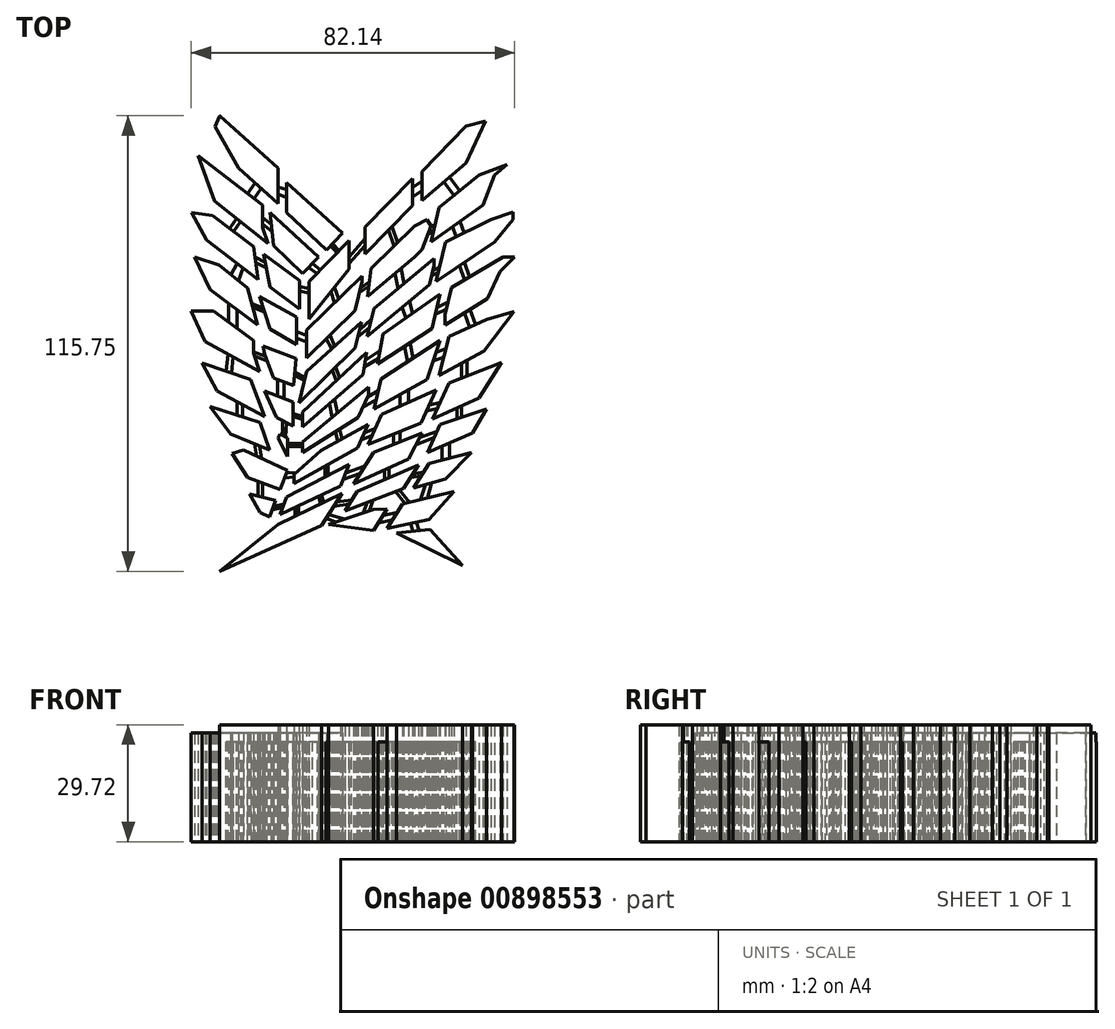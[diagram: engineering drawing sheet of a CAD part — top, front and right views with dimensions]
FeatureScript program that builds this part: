
annotation { "Feature Type Name" : "Feature", "Feature Type Description" : "" }
export const myFeature = defineFeature(function(context is Context, id is Id, definition is map)
    precondition{}
    {
        {
            var Q0;
            Q0=qCreatedBy(makeId("Top.planeOp"),FACE);
            var sketch = newSketch(context, id + "F0", { "sketchPlane" : qUnion([Q0])});
            skLineSegment(sketch, "E0", {"start": v(16.1, 33.24) * mm, "end": v(4.06, 20.9) * mm});
            skLineSegment(sketch, "E1", {"start": v(4.06, 20.9) * mm, "end": v(4.06, 27.82) * mm});
            skLineSegment(sketch, "E2", {"start": v(4.06, 27.82) * mm, "end": v(16.1, 40.16) * mm});
            skLineSegment(sketch, "E3", {"start": v(16.1, 40.16) * mm, "end": v(16.1, 33.24) * mm});
            skLineSegment(sketch, "E4", {"start": v(18.5, 34.46) * mm, "end": v(29.69, 44) * mm});
            skLineSegment(sketch, "E5", {"start": v(29.69, 44) * mm, "end": v(34.61, 54.74) * mm});
            skLineSegment(sketch, "E6", {"start": v(34.61, 54.74) * mm, "end": v(29.69, 53.4) * mm});
            skLineSegment(sketch, "E7", {"start": v(29.69, 53.4) * mm, "end": v(18.5, 41.94) * mm});
            skLineSegment(sketch, "E8", {"start": v(18.5, 41.94) * mm, "end": v(18.5, 34.46) * mm});
            skLineSegment(sketch, "E9", {"start": v(0, 17.06) * mm, "end": v(0, 24.37) * mm});
            skLineSegment(sketch, "E10", {"start": v(0, 24.37) * mm, "end": v(-10.2, 13.91) * mm});
            skLineSegment(sketch, "E11", {"start": v(-10.2, 13.91) * mm, "end": v(-10.2, 4.4) * mm});
            skLineSegment(sketch, "E12", {"start": v(-10.2, 4.4) * mm, "end": v(0, 17.06) * mm});
            skLineSegment(sketch, "E13", {"start": v(3.27, 13.98) * mm, "end": v(1.51, 6.57) * mm});
            skLineSegment(sketch, "E14", {"start": v(1.51, 6.57) * mm, "end": v(-10.85, -5.49) * mm});
            skLineSegment(sketch, "E15", {"start": v(-10.85, -5.49) * mm, "end": v(-10.85, 1.62) * mm});
            skLineSegment(sketch, "E16", {"start": v(-10.85, 1.62) * mm, "end": v(3.27, 15.38) * mm});
            skLineSegment(sketch, "E17", {"start": v(3.27, 15.38) * mm, "end": v(3.27, 13.98) * mm});
            skLineSegment(sketch, "E18", {"start": v(16.55, 28) * mm, "end": v(5.55, 17.27) * mm});
            skLineSegment(sketch, "E19", {"start": v(5.55, 17.27) * mm, "end": v(4.6, 10.07) * mm});
            skLineSegment(sketch, "E20", {"start": v(4.6, 10.07) * mm, "end": v(16.55, 20.16) * mm});
            skLineSegment(sketch, "E21", {"start": v(16.55, 20.16) * mm, "end": v(18.49, 22.05) * mm});
            skLineSegment(sketch, "E22", {"start": v(18.49, 22.05) * mm, "end": v(20.78, 28) * mm});
            skLineSegment(sketch, "E23", {"start": v(20.78, 28) * mm, "end": v(19.75, 29.75) * mm});
            skLineSegment(sketch, "E24", {"start": v(22.84, 32.73) * mm, "end": v(20.78, 24) * mm});
            skLineSegment(sketch, "E25", {"start": v(20.78, 24) * mm, "end": v(34.05, 33.4) * mm});
            skLineSegment(sketch, "E26", {"start": v(34.05, 33.4) * mm, "end": v(36.97, 40.99) * mm});
            skLineSegment(sketch, "E27", {"start": v(36.97, 40.99) * mm, "end": v(40.07, 43.63) * mm});
            skLineSegment(sketch, "E28", {"start": v(40.07, 43.63) * mm, "end": v(32.98, 40.99) * mm});
            skLineSegment(sketch, "E29", {"start": v(32.98, 40.99) * mm, "end": v(22.84, 32.73) * mm});
            skLineSegment(sketch, "E30", {"start": v(24.46, 24) * mm, "end": v(22.1, 13.98) * mm});
            skLineSegment(sketch, "E31", {"start": v(22.1, 13.98) * mm, "end": v(36.97, 24) * mm});
            skLineSegment(sketch, "E32", {"start": v(36.97, 24) * mm, "end": v(41.6, 29.75) * mm});
            skLineSegment(sketch, "E33", {"start": v(24.46, 24) * mm, "end": v(36, 29.75) * mm});
            skLineSegment(sketch, "E34", {"start": v(36, 29.75) * mm, "end": v(41.6, 31.62) * mm});
            skLineSegment(sketch, "E35", {"start": v(41.6, 31.62) * mm, "end": v(41.6, 29.75) * mm});
            skLineSegment(sketch, "E36", {"start": v(6.35, 7.12) * mm, "end": v(4.57, 0) * mm});
            skLineSegment(sketch, "E37", {"start": v(4.57, 0) * mm, "end": v(20.38, 13.16) * mm});
            skLineSegment(sketch, "E38", {"start": v(20.38, 13.16) * mm, "end": v(21.53, 18.02) * mm});
            skLineSegment(sketch, "E39", {"start": v(21.53, 18.02) * mm, "end": v(21.53, 19.72) * mm});
            skLineSegment(sketch, "E40", {"start": v(21.53, 19.72) * mm, "end": v(6.35, 7.12) * mm});
            skLineSegment(sketch, "E41", {"start": v(-10.85, -8.86) * mm, "end": v(-12.74, -16.88) * mm});
            skLineSegment(sketch, "E42", {"start": v(-12.74, -16.88) * mm, "end": v(1.52, -2.98) * mm});
            skLineSegment(sketch, "E43", {"start": v(1.52, -2.98) * mm, "end": v(3.1, 3.67) * mm});
            skLineSegment(sketch, "E44", {"start": v(3.1, 3.67) * mm, "end": v(-10.85, -8.86) * mm});
            skLineSegment(sketch, "E45", {"start": v(4.35, -4.15) * mm, "end": v(-11.88, -19.15) * mm});
            skLineSegment(sketch, "E46", {"start": v(-11.88, -19.15) * mm, "end": v(-11.88, -23.05) * mm});
            skLineSegment(sketch, "E47", {"start": v(-11.88, -23.05) * mm, "end": v(3.53, -9.7) * mm});
            skLineSegment(sketch, "E48", {"start": v(3.53, -9.7) * mm, "end": v(4.35, -4.15) * mm});
            skLineSegment(sketch, "E49", {"start": v(7.23, -7.03) * mm, "end": v(21, 2.01) * mm});
            skLineSegment(sketch, "E50", {"start": v(21, 2.01) * mm, "end": v(23.06, 10.75) * mm});
            skLineSegment(sketch, "E51", {"start": v(23.06, 10.75) * mm, "end": v(8.65, 0.6) * mm});
            skLineSegment(sketch, "E52", {"start": v(8.65, 0.6) * mm, "end": v(7.23, -7.03) * mm});
            skLineSegment(sketch, "E53", {"start": v(26.04, 12.46) * mm, "end": v(24.4, 5.55) * mm});
            skLineSegment(sketch, "E54", {"start": v(24.4, 5.55) * mm, "end": v(24.4, 2.84) * mm});
            skLineSegment(sketch, "E55", {"start": v(24.4, 2.84) * mm, "end": v(35.15, 9.68) * mm});
            skLineSegment(sketch, "E56", {"start": v(35.15, 9.68) * mm, "end": v(36.57, 12.76) * mm});
            skLineSegment(sketch, "E57", {"start": v(36.57, 12.76) * mm, "end": v(38.28, 16.49) * mm});
            skLineSegment(sketch, "E58", {"start": v(38.28, 16.49) * mm, "end": v(42.02, 20.14) * mm});
            skLineSegment(sketch, "E59", {"start": v(42.02, 20.14) * mm, "end": v(39.02, 20.14) * mm});
            skLineSegment(sketch, "E60", {"start": v(39.02, 20.14) * mm, "end": v(26.04, 12.46) * mm});
            skLineSegment(sketch, "E61", {"start": v(-11.84, -29.54) * mm, "end": v(2.25, -20.58) * mm});
            skLineSegment(sketch, "E62", {"start": v(2.25, -20.58) * mm, "end": v(4.88, -14.85) * mm});
            skLineSegment(sketch, "E63", {"start": v(4.88, -14.85) * mm, "end": v(4.88, -12.89) * mm});
            skLineSegment(sketch, "E64", {"start": v(4.88, -12.89) * mm, "end": v(-11.86, -26.82) * mm});
            skLineSegment(sketch, "E65", {"start": v(8.15, -10.8) * mm, "end": v(6.36, -18.42) * mm});
            skLineSegment(sketch, "E66", {"start": v(6.36, -18.42) * mm, "end": v(19.76, -10.9) * mm});
            skLineSegment(sketch, "E67", {"start": v(19.76, -10.9) * mm, "end": v(23.06, -1.06) * mm});
            skLineSegment(sketch, "E68", {"start": v(23.06, -1.06) * mm, "end": v(8.15, -10.8) * mm});
            skLineSegment(sketch, "E69", {"start": v(25.35, 0) * mm, "end": v(22.87, -9.98) * mm});
            skLineSegment(sketch, "E70", {"start": v(22.87, -9.98) * mm, "end": v(34.26, -3.66) * mm});
            skLineSegment(sketch, "E71", {"start": v(34.26, -3.66) * mm, "end": v(41.93, 6.3) * mm});
            skLineSegment(sketch, "E72", {"start": v(41.93, 6.3) * mm, "end": v(34.89, 4.32) * mm});
            skLineSegment(sketch, "E73", {"start": v(34.89, 4.32) * mm, "end": v(25.35, 0) * mm});
            skLineSegment(sketch, "E74", {"start": v(-14, -37.38) * mm, "end": v(2.06, -28.36) * mm});
            skLineSegment(sketch, "E75", {"start": v(2.06, -28.36) * mm, "end": v(4.81, -22.38) * mm});
            skLineSegment(sketch, "E76", {"start": v(4.81, -22.38) * mm, "end": v(-7.2, -28.98) * mm});
            skLineSegment(sketch, "E77", {"start": v(-7.2, -28.98) * mm, "end": v(-14, -35.04) * mm});
            skLineSegment(sketch, "E78", {"start": v(-14, -35.04) * mm, "end": v(-14, -37.38) * mm});
            skLineSegment(sketch, "E79", {"start": v(8.24, -19.84) * mm, "end": v(4.76, -27.42) * mm});
            skLineSegment(sketch, "E80", {"start": v(4.76, -27.42) * mm, "end": v(18.25, -22.06) * mm});
            skLineSegment(sketch, "E81", {"start": v(18.25, -22.06) * mm, "end": v(22.1, -13.66) * mm});
            skLineSegment(sketch, "E82", {"start": v(22.1, -13.66) * mm, "end": v(8.24, -19.84) * mm});
            skLineSegment(sketch, "E83", {"start": v(25.35, -11.8) * mm, "end": v(21.15, -20.96) * mm});
            skLineSegment(sketch, "E84", {"start": v(21.15, -20.96) * mm, "end": v(32.96, -15.63) * mm});
            skLineSegment(sketch, "E85", {"start": v(32.96, -15.63) * mm, "end": v(38.64, -6.61) * mm});
            skLineSegment(sketch, "E86", {"start": v(38.64, -6.61) * mm, "end": v(25.35, -11.8) * mm});
            skLineSegment(sketch, "E87", {"start": v(-11.86, -26.82) * mm, "end": v(-11.84, -29.54) * mm});
            skLineSegment(sketch, "E88", {"start": v(-15.86, -40.84) * mm, "end": v(-17.59, -45.3) * mm});
            skLineSegment(sketch, "E89", {"start": v(-17.59, -45.3) * mm, "end": v(-2.26, -38) * mm});
            skLineSegment(sketch, "E90", {"start": v(-2.26, -38) * mm, "end": v(0, -32.56) * mm});
            skLineSegment(sketch, "E91", {"start": v(0, -32.56) * mm, "end": v(-15.86, -40.84) * mm});
            skLineSegment(sketch, "E92", {"start": v(6.14, -29.54) * mm, "end": v(1.07, -37.5) * mm});
            skLineSegment(sketch, "E93", {"start": v(1.07, -37.5) * mm, "end": v(15.04, -31.2) * mm});
            skLineSegment(sketch, "E94", {"start": v(15.04, -31.2) * mm, "end": v(18.5, -24.53) * mm});
            skLineSegment(sketch, "E95", {"start": v(18.5, -24.53) * mm, "end": v(6.14, -29.54) * mm});
            skLineSegment(sketch, "E96", {"start": v(23.07, -22.43) * mm, "end": v(19.86, -29.54) * mm});
            skLineSegment(sketch, "E97", {"start": v(19.86, -29.54) * mm, "end": v(31.35, -24.53) * mm});
            skLineSegment(sketch, "E98", {"start": v(31.35, -24.53) * mm, "end": v(34.93, -18.48) * mm});
            skLineSegment(sketch, "E99", {"start": v(34.93, -18.48) * mm, "end": v(23.07, -22.43) * mm});
            skLineSegment(sketch, "E100", {"start": v(-18.13, -47.75) * mm, "end": v(-32.87, -59.68) * mm});
            skLineSegment(sketch, "E101", {"start": v(-32.87, -59.68) * mm, "end": v(-6.98, -48) * mm});
            skLineSegment(sketch, "E102", {"start": v(-6.98, -48) * mm, "end": v(-1.85, -39.94) * mm});
            skLineSegment(sketch, "E103", {"start": v(-1.85, -39.94) * mm, "end": v(-18.13, -47.75) * mm});
            skLineSegment(sketch, "E104", {"start": v(2.02, -39.4) * mm, "end": v(-1.11, -44.32) * mm});
            skLineSegment(sketch, "E105", {"start": v(-1.11, -44.32) * mm, "end": v(13.81, -38.66) * mm});
            skLineSegment(sketch, "E106", {"start": v(13.81, -38.66) * mm, "end": v(17.6, -32.7) * mm});
            skLineSegment(sketch, "E107", {"start": v(17.6, -32.7) * mm, "end": v(2.02, -39.4) * mm});
            skLineSegment(sketch, "E108", {"start": v(20.33, -32.27) * mm, "end": v(16.34, -38.54) * mm});
            skLineSegment(sketch, "E109", {"start": v(16.34, -38.54) * mm, "end": v(24.5, -36.2) * mm});
            skLineSegment(sketch, "E110", {"start": v(24.5, -36.2) * mm, "end": v(31.02, -29.54) * mm});
            skLineSegment(sketch, "E111", {"start": v(31.02, -29.54) * mm, "end": v(20.33, -32.27) * mm});
            skLineSegment(sketch, "E112", {"start": v(9.64, -43.82) * mm, "end": v(6.14, -49.32) * mm});
            skLineSegment(sketch, "E113", {"start": v(6.14, -49.32) * mm, "end": v(-5.23, -47.75) * mm});
            skLineSegment(sketch, "E114", {"start": v(-5.23, -47.75) * mm, "end": v(6.14, -43.94) * mm});
            skLineSegment(sketch, "E115", {"start": v(6.14, -43.94) * mm, "end": v(9.64, -43.82) * mm});
            skLineSegment(sketch, "E116", {"start": v(13.57, -42.6) * mm, "end": v(9.64, -48.78) * mm});
            skLineSegment(sketch, "E117", {"start": v(9.64, -48.78) * mm, "end": v(20.33, -46.52) * mm});
            skLineSegment(sketch, "E118", {"start": v(20.33, -46.52) * mm, "end": v(26.6, -39.4) * mm});
            skLineSegment(sketch, "E119", {"start": v(26.6, -39.4) * mm, "end": v(13.57, -42.6) * mm});
            skLineSegment(sketch, "E120", {"start": v(-34.07, 53.36) * mm, "end": v(-28.12, 42.75) * mm});
            skLineSegment(sketch, "E121", {"start": v(-28.12, 42.75) * mm, "end": v(-18.13, 33.7) * mm});
            skLineSegment(sketch, "E122", {"start": v(-18.13, 33.7) * mm, "end": v(-18.13, 42.8) * mm});
            skLineSegment(sketch, "E123", {"start": v(-18.13, 42.8) * mm, "end": v(-32.88, 56.07) * mm});
            skLineSegment(sketch, "E124", {"start": v(-32.88, 56.07) * mm, "end": v(-34.07, 53.36) * mm});
            skLineSegment(sketch, "E125", {"start": v(-15.86, 39.07) * mm, "end": v(-15.86, 31.48) * mm});
            skLineSegment(sketch, "E126", {"start": v(-15.86, 31.48) * mm, "end": v(-5.79, 21.95) * mm});
            skLineSegment(sketch, "E127", {"start": v(-5.79, 21.95) * mm, "end": v(-1.74, 26.22) * mm});
            skLineSegment(sketch, "E128", {"start": v(-1.74, 26.22) * mm, "end": v(-15.86, 39.07) * mm});
            skLineSegment(sketch, "E129", {"start": v(-20.08, 31.48) * mm, "end": v(-7.72, 20.16) * mm});
            skLineSegment(sketch, "E130", {"start": v(-7.72, 20.16) * mm, "end": v(-11.84, 15.94) * mm});
            skLineSegment(sketch, "E131", {"start": v(-11.84, 15.94) * mm, "end": v(-19.21, 23.13) * mm});
            skLineSegment(sketch, "E132", {"start": v(-19.21, 23.13) * mm, "end": v(-20.08, 31.48) * mm});
            skLineSegment(sketch, "E133", {"start": v(-34.22, 34.33) * mm, "end": v(-38.4, 45.92) * mm});
            skLineSegment(sketch, "E134", {"start": v(-22.01, 27.63) * mm, "end": v(-20.55, 23.57) * mm});
            skLineSegment(sketch, "E135", {"start": v(-20.55, 23.57) * mm, "end": v(-34.22, 34.33) * mm});
            skLineSegment(sketch, "E136", {"start": v(-22.01, 27.63) * mm, "end": v(-22.01, 33.36) * mm});
            skLineSegment(sketch, "E137", {"start": v(-22.01, 33.36) * mm, "end": v(-38.4, 45.92) * mm});
            skLineSegment(sketch, "E138", {"start": v(-24.3, 22.86) * mm, "end": v(-23.16, 14.47) * mm});
            skLineSegment(sketch, "E139", {"start": v(-23.16, 14.47) * mm, "end": v(-36.23, 24.45) * mm});
            skLineSegment(sketch, "E140", {"start": v(-36.23, 24.45) * mm, "end": v(-40.02, 31.51) * mm});
            skLineSegment(sketch, "E141", {"start": v(-40.02, 31.51) * mm, "end": v(-34.73, 30.72) * mm});
            skLineSegment(sketch, "E142", {"start": v(-34.73, 30.72) * mm, "end": v(-24.3, 22.86) * mm});
            skLineSegment(sketch, "E143", {"start": v(-21.72, 20.9) * mm, "end": v(-20.13, 12.57) * mm});
            skLineSegment(sketch, "E144", {"start": v(-20.13, 12.57) * mm, "end": v(-12.65, 6.93) * mm});
            skLineSegment(sketch, "E145", {"start": v(-12.65, 6.93) * mm, "end": v(-12.65, 14.16) * mm});
            skLineSegment(sketch, "E146", {"start": v(-12.65, 14.16) * mm, "end": v(-21.72, 20.9) * mm});
            skLineSegment(sketch, "E147", {"start": v(-22.78, 10.1) * mm, "end": v(-20.13, 1.88) * mm});
            skLineSegment(sketch, "E148", {"start": v(-20.13, 1.88) * mm, "end": v(-13.4, -2.01) * mm});
            skLineSegment(sketch, "E149", {"start": v(-13.4, -2.01) * mm, "end": v(-13.4, 4.88) * mm});
            skLineSegment(sketch, "E150", {"start": v(-13.4, 4.88) * mm, "end": v(-22.78, 10.1) * mm});
            skLineSegment(sketch, "E151", {"start": v(-25.78, 12.3) * mm, "end": v(-23.3, 2.87) * mm});
            skLineSegment(sketch, "E152", {"start": v(-23.3, 2.87) * mm, "end": v(-35.28, 11.91) * mm});
            skLineSegment(sketch, "E153", {"start": v(-35.28, 11.91) * mm, "end": v(-39.33, 20.22) * mm});
            skLineSegment(sketch, "E154", {"start": v(-39.33, 20.22) * mm, "end": v(-33.04, 18.07) * mm});
            skLineSegment(sketch, "E155", {"start": v(-33.04, 18.07) * mm, "end": v(-25.78, 12.3) * mm});
            skLineSegment(sketch, "E156", {"start": v(-24.3, -4.2) * mm, "end": v(-22.78, -8.95) * mm});
            skLineSegment(sketch, "E157", {"start": v(-22.78, -8.95) * mm, "end": v(-36.62, -1.25) * mm});
            skLineSegment(sketch, "E158", {"start": v(-36.62, -1.25) * mm, "end": v(-40.12, 6.45) * mm});
            skLineSegment(sketch, "E159", {"start": v(-40.12, 6.45) * mm, "end": v(-34.4, 6.45) * mm});
            skLineSegment(sketch, "E160", {"start": v(-34.4, 6.45) * mm, "end": v(-24.3, -1.06) * mm});
            skLineSegment(sketch, "E161", {"start": v(-24.3, -1.06) * mm, "end": v(-24.3, -4.2) * mm});
            skLineSegment(sketch, "E162", {"start": v(-21.55, -4.41) * mm, "end": v(-19.24, -10.6) * mm});
            skLineSegment(sketch, "E163", {"start": v(-19.24, -10.6) * mm, "end": v(-14.15, -12.46) * mm});
            skLineSegment(sketch, "E164", {"start": v(-14.15, -12.46) * mm, "end": v(-13.5, -5.62) * mm});
            skLineSegment(sketch, "E165", {"start": v(-13.5, -5.62) * mm, "end": v(-21.82, -2.38) * mm});
            skLineSegment(sketch, "E166", {"start": v(-21.82, -2.38) * mm, "end": v(-21.55, -4.41) * mm});
            skLineSegment(sketch, "E167", {"start": v(-21.55, -13.86) * mm, "end": v(-18.48, -20.65) * mm});
            skLineSegment(sketch, "E168", {"start": v(-18.48, -20.65) * mm, "end": v(-14.3, -22.8) * mm});
            skLineSegment(sketch, "E169", {"start": v(-14.3, -16.62) * mm, "end": v(-21.55, -13.86) * mm});
            skLineSegment(sketch, "E170", {"start": v(-37.4, -6.81) * mm, "end": v(-33.52, -13.86) * mm});
            skLineSegment(sketch, "E171", {"start": v(-33.52, -13.86) * mm, "end": v(-21.55, -20.4) * mm});
            skLineSegment(sketch, "E172", {"start": v(-21.55, -20.4) * mm, "end": v(-25.12, -10.95) * mm});
            skLineSegment(sketch, "E173", {"start": v(-25.12, -10.95) * mm, "end": v(-37.4, -6.81) * mm});
            skLineSegment(sketch, "E174", {"start": v(-17.57, -24.82) * mm, "end": v(-15.6, -25.84) * mm});
            skLineSegment(sketch, "E175", {"start": v(-15.6, -25.84) * mm, "end": v(-15.6, -30.49) * mm});
            skLineSegment(sketch, "E176", {"start": v(-17.57, -24.82) * mm, "end": v(-18.1, -25.87) * mm});
            skLineSegment(sketch, "E177", {"start": v(-18.1, -25.87) * mm, "end": v(-15.6, -30.49) * mm});
            skLineSegment(sketch, "E178", {"start": v(-20.25, -28.9) * mm, "end": v(-22.65, -21.85) * mm});
            skLineSegment(sketch, "E179", {"start": v(-22.65, -21.85) * mm, "end": v(-35.36, -17.78) * mm});
            skLineSegment(sketch, "E180", {"start": v(-35.36, -17.78) * mm, "end": v(-30.13, -24.82) * mm});
            skLineSegment(sketch, "E181", {"start": v(-30.13, -24.82) * mm, "end": v(-20.25, -28.9) * mm});
            skLineSegment(sketch, "E182", {"start": v(-15.6, -34.12) * mm, "end": v(-17.57, -38.88) * mm});
            skLineSegment(sketch, "E183", {"start": v(-17.57, -38.88) * mm, "end": v(-25.8, -35.89) * mm});
            skLineSegment(sketch, "E184", {"start": v(-25.8, -35.89) * mm, "end": v(-29.78, -29.8) * mm});
            skLineSegment(sketch, "E185", {"start": v(-29.78, -29.8) * mm, "end": v(-26.8, -28.9) * mm});
            skLineSegment(sketch, "E186", {"start": v(-26.8, -28.9) * mm, "end": v(-15.6, -34.12) * mm});
            skLineSegment(sketch, "E187", {"start": v(-18.73, -41.72) * mm, "end": v(-20.25, -45.91) * mm});
            skLineSegment(sketch, "E188", {"start": v(-20.25, -45.91) * mm, "end": v(-22.6, -44.7) * mm});
            skLineSegment(sketch, "E189", {"start": v(-22.6, -44.7) * mm, "end": v(-25.25, -39.97) * mm});
            skLineSegment(sketch, "E190", {"start": v(-25.25, -39.97) * mm, "end": v(-18.73, -41.72) * mm});
            skLineSegment(sketch, "E191", {"start": v(11.97, -49.96) * mm, "end": v(20.57, -49.05) * mm});
            skLineSegment(sketch, "E192", {"start": v(20.57, -49.05) * mm, "end": v(28.76, -58.25) * mm});
            skLineSegment(sketch, "E193", {"start": v(28.76, -58.25) * mm, "end": v(11.97, -49.96) * mm});
            skLineSegment(sketch, "E194", {"start": v(-11.88, -23.05) * mm, "end": v(-11.86, -26.82) * mm});
            skLineSegment(sketch, "E195", {"start": v(-12.74, -16.88) * mm, "end": v(-11.88, -19.15) * mm});
            skLineSegment(sketch, "E196", {"start": v(-10.68, -5.38) * mm, "end": v(-10.85, -8.86) * mm});
            skLineSegment(sketch, "E197", {"start": v(-14, -37.38) * mm, "end": v(-15.86, -40.84) * mm});
            skLineSegment(sketch, "E198", {"start": v(16.55, 28) * mm, "end": v(19.75, 29.75) * mm});
            skLineSegment(sketch, "E199", {"start": v(4.57, 0) * mm, "end": v(1.52, -2.98) * mm});
            skLineSegment(sketch, "E200", {"start": v(22.1, -13.66) * mm, "end": v(25.35, -11.8) * mm});
            skLineSegment(sketch, "E201", {"start": v(-17.59, -45.3) * mm, "end": v(-18.13, -47.75) * mm});
            skLineSegment(sketch, "E202", {"start": v(24.4, 2.84) * mm, "end": v(25.35, 0) * mm});
            skLineSegment(sketch, "E203", {"start": v(-14.3, -16.62) * mm, "end": v(-14.3, -22.8) * mm});
            skLineSegment(sketch, "E204.bottom", {"start": v(-32.9, 56.04) * mm, "end": v(-32.85, 56.04) * mm});
            skSolve(sketch);
        }
        {
            var Q0;
            Q0=makeQuery(id+"F0.imprint","IMPRINT",FACE,{"disambiguationData":[TD([[makeQuery(id+"F0.imprint","IMPRINT",EDGE,{"derivedFrom":sQuery(id+"F0.wireOp",EDGE,"E170")}),1.0]])]});
            var Q1;
            Q1=makeQuery(id+"F0.imprint","IMPRINT",FACE,{"disambiguationData":[TD([[makeQuery(id+"F0.imprint","IMPRINT",EDGE,{"derivedFrom":sQuery(id+"F0.wireOp",EDGE,"E191")}),-1.0]])]});
            var Q2;
            Q2=makeQuery(id+"F0.imprint","IMPRINT",FACE,{"disambiguationData":[TD([[makeQuery(id+"F0.imprint","IMPRINT",EDGE,{"derivedFrom":sQuery(id+"F0.wireOp",EDGE,"E4")}),1.0]])]});
            var Q3;
            Q3=makeQuery(id+"F0.imprint","IMPRINT",FACE,{"disambiguationData":[TD([[makeQuery(id+"F0.imprint","IMPRINT",EDGE,{"derivedFrom":sQuery(id+"F0.wireOp",EDGE,"E69")}),1.0]])]});
            var Q4;
            Q4=makeQuery(id+"F0.imprint","IMPRINT",FACE,{"disambiguationData":[TD([[makeQuery(id+"F0.imprint","IMPRINT",EDGE,{"derivedFrom":sQuery(id+"F0.wireOp",EDGE,"E83")}),1.0]])]});
            var Q5;
            Q5=makeQuery(id+"F0.imprint","IMPRINT",FACE,{"disambiguationData":[TD([[makeQuery(id+"F0.imprint","IMPRINT",EDGE,{"derivedFrom":sQuery(id+"F0.wireOp",EDGE,"E96")}),1.0]])]});
            var Q6;
            Q6=makeQuery(id+"F0.imprint","IMPRINT",FACE,{"disambiguationData":[TD([[makeQuery(id+"F0.imprint","IMPRINT",EDGE,{"derivedFrom":sQuery(id+"F0.wireOp",EDGE,"E100")}),1.0]])]});
            var Q7;
            Q7=makeQuery(id+"F0.imprint","IMPRINT",FACE,{"disambiguationData":[TD([[makeQuery(id+"F0.imprint","IMPRINT",EDGE,{"derivedFrom":sQuery(id+"F0.wireOp",EDGE,"E108")}),1.0]])]});
            var Q8;
            Q8=makeQuery(id+"F0.imprint","IMPRINT",FACE,{"disambiguationData":[TD([[makeQuery(id+"F0.imprint","IMPRINT",EDGE,{"derivedFrom":sQuery(id+"F0.wireOp",EDGE,"E112")}),-1.0]])]});
            var Q9;
            Q9=makeQuery(id+"F0.imprint","IMPRINT",FACE,{"disambiguationData":[TD([[makeQuery(id+"F0.imprint","IMPRINT",EDGE,{"derivedFrom":sQuery(id+"F0.wireOp",EDGE,"E116")}),1.0]])]});
            var Q10;
            Q10=makeQuery(id+"F0.imprint","IMPRINT",FACE,{"disambiguationData":[TD([[makeQuery(id+"F0.imprint","IMPRINT",EDGE,{"derivedFrom":sQuery(id+"F0.wireOp",EDGE,"E120")}),1.0]])]});
            var Q11;
            Q11=makeQuery(id+"F0.imprint","IMPRINT",FACE,{"disambiguationData":[TD([[makeQuery(id+"F0.imprint","IMPRINT",EDGE,{"derivedFrom":sQuery(id+"F0.wireOp",EDGE,"E156")}),-1.0]])]});
            var Q12;
            Q12=makeQuery(id+"F0.imprint","IMPRINT",FACE,{"disambiguationData":[TD([[makeQuery(id+"F0.imprint","IMPRINT",EDGE,{"derivedFrom":sQuery(id+"F0.wireOp",EDGE,"E178")}),1.0]])]});
            var Q13;
            Q13=makeQuery(id+"F0.imprint","IMPRINT",FACE,{"disambiguationData":[TD([[makeQuery(id+"F0.imprint","IMPRINT",EDGE,{"derivedFrom":sQuery(id+"F0.wireOp",EDGE,"E187")}),-1.0]])]});
            var Q14;
            Q14=makeQuery(id+"F0.imprint","IMPRINT",FACE,{"disambiguationData":[TD([[makeQuery(id+"F0.imprint","IMPRINT",EDGE,{"derivedFrom":sQuery(id+"F0.wireOp",EDGE,"E0")}),-1.0]])]});
            var Q15;
            Q15=makeQuery(id+"F0.imprint","IMPRINT",FACE,{"disambiguationData":[TD([[makeQuery(id+"F0.imprint","IMPRINT",EDGE,{"derivedFrom":sQuery(id+"F0.wireOp",EDGE,"E24")}),1.0]])]});
            var Q16;
            Q16=makeQuery(id+"F0.imprint","IMPRINT",FACE,{"disambiguationData":[TD([[makeQuery(id+"F0.imprint","IMPRINT",EDGE,{"derivedFrom":sQuery(id+"F0.wireOp",EDGE,"E30")}),1.0]])]});
            var Q17;
            Q17=makeQuery(id+"F0.imprint","IMPRINT",FACE,{"disambiguationData":[TD([[makeQuery(id+"F0.imprint","IMPRINT",EDGE,{"derivedFrom":sQuery(id+"F0.wireOp",EDGE,"E53")}),1.0]])]});
            var Q18;
            Q18=makeQuery(id+"F0.imprint","IMPRINT",FACE,{"disambiguationData":[TD([[makeQuery(id+"F0.imprint","IMPRINT",EDGE,{"derivedFrom":sQuery(id+"F0.wireOp",EDGE,"E125")}),1.0]])]});
            var Q19;
            {var subQ1=sQuery(id+"F0.wireOp",EDGE,"E133");Q19=makeQuery(id+"F0.imprint","IMPRINT",FACE,{"disambiguationData":[TD([[makeQuery(id+"F0.imprint","IMPRINT",EDGE,{"derivedFrom":subQ1}),-1.0]])]});}
            var Q20;
            Q20=makeQuery(id+"F0.imprint","IMPRINT",FACE,{"disambiguationData":[TD([[makeQuery(id+"F0.imprint","IMPRINT",EDGE,{"derivedFrom":sQuery(id+"F0.wireOp",EDGE,"E138")}),-1.0]])]});
            var Q21;
            Q21=makeQuery(id+"F0.imprint","IMPRINT",FACE,{"disambiguationData":[TD([[makeQuery(id+"F0.imprint","IMPRINT",EDGE,{"derivedFrom":sQuery(id+"F0.wireOp",EDGE,"E151")}),-1.0]])]});
            var Q22;
            Q22=makeQuery(id+"F0.imprint","IMPRINT",FACE,{"disambiguationData":[TD([[makeQuery(id+"F0.imprint","IMPRINT",EDGE,{"derivedFrom":sQuery(id+"F0.wireOp",EDGE,"E182")}),-1.0]])]});
            var Q23;
            Q23=makeQuery(id+"F0.imprint","IMPRINT",FACE,{"disambiguationData":[TD([[makeQuery(id+"F0.imprint","IMPRINT",EDGE,{"derivedFrom":sQuery(id+"F0.wireOp",EDGE,"E88")}),-1.0]])]});
            var Q24;
            Q24=makeQuery(id+"F0.imprint","IMPRINT",FACE,{"disambiguationData":[TD([[makeQuery(id+"F0.imprint","IMPRINT",EDGE,{"derivedFrom":sQuery(id+"F0.wireOp",EDGE,"Hd1NYOsB-rz69-P5dz-xRzD-SZfXTA0eVR0r")}),-1.0]])]});
            var Q25;
            Q25=makeQuery(id+"F0.imprint","IMPRINT",FACE,{"disambiguationData":[TD([[makeQuery(id+"F0.imprint","IMPRINT",EDGE,{"derivedFrom":sQuery(id+"F0.wireOp",EDGE,"LXoHO3Um-HMFk-hWAO-TxCi-RrEVqA140TyF")}),-1.0]])]});
            var Q26;
            Q26=makeQuery(id+"F0.imprint","IMPRINT",FACE,{"disambiguationData":[TD([[makeQuery(id+"F0.imprint","IMPRINT",EDGE,{"derivedFrom":sQuery(id+"F0.wireOp",EDGE,"s4iQujFb-FTHa-1j17-edHK-8T7tGA8HVips")}),-1.0]])]});
            var Q27;
            Q27=makeQuery(id+"F0.imprint","IMPRINT",FACE,{"disambiguationData":[TD([[makeQuery(id+"F0.imprint","IMPRINT",EDGE,{"derivedFrom":sQuery(id+"F0.wireOp",EDGE,"Gbdayy7W-T8TN-iNEz-qSY6-jhz4T1zxVgPG")}),1.0]])]});
            var Q28;
            Q28=makeQuery(id+"F0.imprint","IMPRINT",FACE,{"disambiguationData":[TD([[makeQuery(id+"F0.imprint","IMPRINT",EDGE,{"derivedFrom":sQuery(id+"F0.wireOp",EDGE,"7w66SsBE-xR8B-FUVp-ku2R-Ja8Xr2Ik3K67")}),-1.0]])]});
            var Q29;
            Q29=makeQuery(id+"F0.imprint","IMPRINT",FACE,{"disambiguationData":[TD([[makeQuery(id+"F0.imprint","IMPRINT",EDGE,{"derivedFrom":sQuery(id+"F0.wireOp",EDGE,"E143")}),1.0]])]});
            var Q30;
            Q30=makeQuery(id+"F0.imprint","IMPRINT",FACE,{"disambiguationData":[TD([[makeQuery(id+"F0.imprint","IMPRINT",EDGE,{"derivedFrom":sQuery(id+"F0.wireOp",EDGE,"E147")}),1.0]])]});
            var Q31;
            Q31=makeQuery(id+"F0.imprint","IMPRINT",FACE,{"disambiguationData":[TD([[makeQuery(id+"F0.imprint","IMPRINT",EDGE,{"derivedFrom":sQuery(id+"F0.wireOp",EDGE,"E162")}),1.0]])]});
            var Q32;
            Q32=makeQuery(id+"F0.imprint","IMPRINT",FACE,{"disambiguationData":[TD([[makeQuery(id+"F0.imprint","IMPRINT",EDGE,{"derivedFrom":sQuery(id+"F0.wireOp",EDGE,"E9")}),1.0]])]});
            var Q33;
            Q33=makeQuery(id+"F0.imprint","IMPRINT",FACE,{"disambiguationData":[TD([[makeQuery(id+"F0.imprint","IMPRINT",EDGE,{"derivedFrom":sQuery(id+"F0.wireOp",EDGE,"tGLAlcHM-KQt4-kowp-IBfW-h8fglPtgRWNQ")}),1.0]])]});
            var Q34;
            Q34=makeQuery(id+"F0.imprint","IMPRINT",FACE,{"disambiguationData":[TD([[makeQuery(id+"F0.imprint","IMPRINT",EDGE,{"derivedFrom":sQuery(id+"F0.wireOp",EDGE,"E13")}),-1.0]])]});
            var Q35;
            Q35=makeQuery(id+"F0.imprint","IMPRINT",FACE,{"disambiguationData":[TD([[makeQuery(id+"F0.imprint","IMPRINT",EDGE,{"derivedFrom":sQuery(id+"F0.wireOp",EDGE,"E36")}),1.0]])]});
            var Q36;
            Q36=makeQuery(id+"F0.imprint","IMPRINT",FACE,{"disambiguationData":[TD([[makeQuery(id+"F0.imprint","IMPRINT",EDGE,{"derivedFrom":sQuery(id+"F0.wireOp",EDGE,"E49")}),1.0]])]});
            var Q37;
            Q37=makeQuery(id+"F0.imprint","IMPRINT",FACE,{"disambiguationData":[TD([[makeQuery(id+"F0.imprint","IMPRINT",EDGE,{"derivedFrom":sQuery(id+"F0.wireOp",EDGE,"E45")}),1.0]])]});
            var Q38;
            Q38=makeQuery(id+"F0.imprint","IMPRINT",FACE,{"disambiguationData":[TD([[makeQuery(id+"F0.imprint","IMPRINT",EDGE,{"derivedFrom":sQuery(id+"F0.wireOp",EDGE,"E41")}),1.0]])]});
            var Q39;
            Q39=makeQuery(id+"F0.imprint","IMPRINT",FACE,{"disambiguationData":[TD([[makeQuery(id+"F0.imprint","IMPRINT",EDGE,{"derivedFrom":sQuery(id+"F0.wireOp",EDGE,"E65")}),1.0]])]});
            var Q40;
            Q40=makeQuery(id+"F0.imprint","IMPRINT",FACE,{"disambiguationData":[TD([[makeQuery(id+"F0.imprint","IMPRINT",EDGE,{"derivedFrom":sQuery(id+"F0.wireOp",EDGE,"E61")}),1.0]])]});
            var Q41;
            Q41=makeQuery(id+"F0.imprint","IMPRINT",FACE,{"disambiguationData":[TD([[makeQuery(id+"F0.imprint","IMPRINT",EDGE,{"derivedFrom":sQuery(id+"F0.wireOp",EDGE,"E79")}),1.0]])]});
            var Q42;
            Q42=makeQuery(id+"F0.imprint","IMPRINT",FACE,{"disambiguationData":[TD([[makeQuery(id+"F0.imprint","IMPRINT",EDGE,{"derivedFrom":sQuery(id+"F0.wireOp",EDGE,"E74")}),1.0]])]});
            var Q43;
            Q43=makeQuery(id+"F0.imprint","IMPRINT",FACE,{"disambiguationData":[TD([[makeQuery(id+"F0.imprint","IMPRINT",EDGE,{"derivedFrom":sQuery(id+"F0.wireOp",EDGE,"E92")}),1.0]])]});
            var Q44;
            Q44=makeQuery(id+"F0.imprint","IMPRINT",FACE,{"disambiguationData":[TD([[makeQuery(id+"F0.imprint","IMPRINT",EDGE,{"derivedFrom":sQuery(id+"F0.wireOp",EDGE,"E18")}),1.0]])]});
            var Q45;
            Q45=makeQuery(id+"F0.imprint","IMPRINT",FACE,{"disambiguationData":[TD([[makeQuery(id+"F0.imprint","IMPRINT",EDGE,{"derivedFrom":sQuery(id+"F0.wireOp",EDGE,"E174")}),-1.0]])]});
            var Q46;
            Q46=makeQuery(id+"F0.imprint","IMPRINT",FACE,{"disambiguationData":[TD([[makeQuery(id+"F0.imprint","IMPRINT",EDGE,{"derivedFrom":sQuery(id+"F0.wireOp",EDGE,"E129")}),-1.0]])]});
            var Q47;
            Q47=makeQuery(id+"F0.imprint","IMPRINT",FACE,{"disambiguationData":[TD([[makeQuery(id+"F0.imprint","IMPRINT",EDGE,{"derivedFrom":sQuery(id+"F0.wireOp",EDGE,"E88")}),1.0]])]});
            var Q48;
            Q48=makeQuery(id+"F0.imprint","IMPRINT",FACE,{"disambiguationData":[TD([[makeQuery(id+"F0.imprint","IMPRINT",EDGE,{"derivedFrom":sQuery(id+"F0.wireOp",EDGE,"E104")}),1.0]])]});
            var Q49;
            Q49=makeQuery(id+"F0.imprint","IMPRINT",FACE,{"disambiguationData":[TD([[makeQuery(id+"F0.imprint","IMPRINT",EDGE,{"derivedFrom":sQuery(id+"F0.wireOp",EDGE,"E167")}),1.0]])]});
            var Q50;
            {var subQ0=sQuery(id+"F0.wireOp",EDGE,"E102");Q50=makeQuery(id+"F0.imprint","IMPRINT",FACE,{"disambiguationData":[TD([[makeQuery(id+"F0.imprint","IMPRINT",EDGE,{"derivedFrom":subQ0}),1.0]])]});}
            extrude(context, id + "F1", {"entities" : qUnion([Q0, Q1, Q2, Q3, Q4, Q5, Q6, Q7, Q8, Q9, Q10, Q11, Q12, Q13, Q14, Q15, Q16, Q17, Q18, Q19, Q20, Q21, Q22, Q23, Q24, Q25, Q26, Q27, Q28, Q29, Q30, Q31, Q32, Q33, Q34, Q35, Q36, Q37, Q38, Q39, Q40, Q41, Q42, Q43, Q44, Q45, Q46, Q47, Q48, Q49, Q50]), "depth" : 29.72 * mm, "offsetDistance" : 25.4 * mm});
        }
        {
            var Q0;
            Q0=qCreatedBy(makeId("Top.planeOp"),FACE);
            var sketch = newSketch(context, id + "F2", { "sketchPlane" : qUnion([Q0])});
            skLineSegment(sketch, "E205", {"start": v(-23.09, 31) * mm, "end": v(-23.58, 29.74) * mm});
            skLineSegment(sketch, "E206", {"start": v(-23.58, 29.74) * mm, "end": v(-17.62, 25.06) * mm});
            skLineSegment(sketch, "E207", {"start": v(-17.62, 25.06) * mm, "end": v(-16.83, 26.06) * mm});
            skLineSegment(sketch, "E208", {"start": v(-16.83, 26.06) * mm, "end": v(-23.09, 31) * mm});
            skLineSegment(sketch, "E209", {"start": v(-23.63, 39.32) * mm, "end": v(-26.94, 34.63) * mm});
            skLineSegment(sketch, "E210", {"start": v(-26.94, 34.63) * mm, "end": v(-25.32, 33.49) * mm});
            skLineSegment(sketch, "E211", {"start": v(-25.32, 33.49) * mm, "end": v(-21.32, 39.14) * mm});
            skLineSegment(sketch, "E212", {"start": v(-21.32, 39.14) * mm, "end": v(-22.68, 40.1) * mm});
            skLineSegment(sketch, "E213", {"start": v(-22.68, 40.1) * mm, "end": v(-23.63, 39.32) * mm});
            skLineSegment(sketch, "E214", {"start": v(-28.02, 30.84) * mm, "end": v(-31.4, 26.06) * mm});
            skLineSegment(sketch, "E215", {"start": v(-31.4, 26.06) * mm, "end": v(-30.33, 25.31) * mm});
            skLineSegment(sketch, "E216", {"start": v(-30.33, 25.31) * mm, "end": v(-27.22, 29.71) * mm});
            skLineSegment(sketch, "E217", {"start": v(-27.22, 29.71) * mm, "end": v(-28.02, 30.84) * mm});
            skLineSegment(sketch, "E218", {"start": v(-27.78, 19.97) * mm, "end": v(-30.66, 14.54) * mm});
            skLineSegment(sketch, "E219", {"start": v(-30.66, 14.54) * mm, "end": v(-28.5, 13.4) * mm});
            skLineSegment(sketch, "E220", {"start": v(-28.5, 13.4) * mm, "end": v(-26.12, 19.25) * mm});
            skLineSegment(sketch, "E221", {"start": v(-26.12, 19.25) * mm, "end": v(-27.78, 19.97) * mm});
            skLineSegment(sketch, "E222", {"start": v(-30.66, 9.75) * mm, "end": v(-30.66, 1.76) * mm});
            skLineSegment(sketch, "E223", {"start": v(-30.66, 1.76) * mm, "end": v(-28.5, 0) * mm});
            skLineSegment(sketch, "E224", {"start": v(-28.5, 0) * mm, "end": v(-28.5, 8.99) * mm});
            skLineSegment(sketch, "E225", {"start": v(-28.5, 8.99) * mm, "end": v(-30.66, 9.75) * mm});
            skLineSegment(sketch, "E226", {"start": v(-30.66, -3.09) * mm, "end": v(-31.48, -10.2) * mm});
            skLineSegment(sketch, "E227", {"start": v(-31.48, -10.2) * mm, "end": v(-29.96, -10.74) * mm});
            skLineSegment(sketch, "E228", {"start": v(-29.96, -10.74) * mm, "end": v(-29.33, -3.54) * mm});
            skLineSegment(sketch, "E229", {"start": v(-29.33, -3.54) * mm, "end": v(-30.66, -3.09) * mm});
            skLineSegment(sketch, "E230", {"start": v(-28.5, -15.32) * mm, "end": v(-28.5, -21.78) * mm});
            skLineSegment(sketch, "E231", {"start": v(-28.5, -21.78) * mm, "end": v(-27.06, -21.9) * mm});
            skLineSegment(sketch, "E232", {"start": v(-27.06, -21.9) * mm, "end": v(-27.06, -15.32) * mm});
            skLineSegment(sketch, "E233", {"start": v(-27.06, -15.32) * mm, "end": v(-28.5, -15.32) * mm});
            skLineSegment(sketch, "E234", {"start": v(-24.24, -26.27) * mm, "end": v(-23.2, -31.99) * mm});
            skLineSegment(sketch, "E235", {"start": v(-23.2, -31.99) * mm, "end": v(-22.05, -32.09) * mm});
            skLineSegment(sketch, "E236", {"start": v(-22.05, -32.09) * mm, "end": v(-23.2, -25.68) * mm});
            skLineSegment(sketch, "E237", {"start": v(-23.2, -25.68) * mm, "end": v(-24.24, -26.27) * mm});
            skLineSegment(sketch, "E238", {"start": v(-23.2, -36.12) * mm, "end": v(-23.2, -41.44) * mm});
            skLineSegment(sketch, "E239", {"start": v(-23.2, -41.44) * mm, "end": v(-22.05, -41.54) * mm});
            skLineSegment(sketch, "E240", {"start": v(-22.05, -41.54) * mm, "end": v(-22.05, -35.74) * mm});
            skLineSegment(sketch, "E241", {"start": v(-22.05, -35.74) * mm, "end": v(-23.2, -36.12) * mm});
            skLineSegment(sketch, "E242", {"start": v(-24.79, 20.59) * mm, "end": v(-19.81, 17.99) * mm});
            skLineSegment(sketch, "E243", {"start": v(-19.81, 17.99) * mm, "end": v(-19.81, 16.74) * mm});
            skLineSegment(sketch, "E244", {"start": v(-19.81, 16.74) * mm, "end": v(-24.79, 19.34) * mm});
            skLineSegment(sketch, "E245", {"start": v(-24.79, 19.34) * mm, "end": v(-24.79, 20.59) * mm});
            skLineSegment(sketch, "E246", {"start": v(-25.74, 8.8) * mm, "end": v(-19.81, 6.44) * mm});
            skLineSegment(sketch, "E247", {"start": v(-19.81, 6.44) * mm, "end": v(-20.15, 5.6) * mm});
            skLineSegment(sketch, "E248", {"start": v(-20.15, 5.6) * mm, "end": v(-25.74, 7.82) * mm});
            skLineSegment(sketch, "E249", {"start": v(-25.74, 7.82) * mm, "end": v(-25.74, 8.8) * mm});
            skLineSegment(sketch, "E250", {"start": v(-25.74, -3.45) * mm, "end": v(-25.74, -4.28) * mm});
            skLineSegment(sketch, "E251", {"start": v(-25.74, -4.28) * mm, "end": v(-19.81, -6.63) * mm});
            skLineSegment(sketch, "E252", {"start": v(-19.81, -6.63) * mm, "end": v(-19.81, -5.48) * mm});
            skLineSegment(sketch, "E253", {"start": v(-19.81, -5.48) * mm, "end": v(-25.74, -3.45) * mm});
            skLineSegment(sketch, "E254", {"start": v(-18.16, -16.2) * mm, "end": v(-18.16, -9.75) * mm});
            skLineSegment(sketch, "E255", {"start": v(-18.16, -9.75) * mm, "end": v(-16.59, -9.75) * mm});
            skLineSegment(sketch, "E256", {"start": v(-16.59, -9.75) * mm, "end": v(-16.59, -17.23) * mm});
            skLineSegment(sketch, "E257", {"start": v(-16.59, -17.23) * mm, "end": v(-18.16, -16.2) * mm});
            skLineSegment(sketch, "E258", {"start": v(-8.85, 10.73) * mm, "end": v(-14.34, 11.9) * mm});
            skLineSegment(sketch, "E259", {"start": v(-14.34, 11.9) * mm, "end": v(-14.34, 13.04) * mm});
            skLineSegment(sketch, "E260", {"start": v(-14.34, 13.04) * mm, "end": v(-9.02, 11.9) * mm});
            skLineSegment(sketch, "E261", {"start": v(-9.02, 11.9) * mm, "end": v(-8.85, 10.73) * mm});
            skLineSegment(sketch, "E262", {"start": v(-9.97, -1.79) * mm, "end": v(-14.38, 0) * mm});
            skLineSegment(sketch, "E263", {"start": v(-14.38, 0) * mm, "end": v(-14.38, 1.63) * mm});
            skLineSegment(sketch, "E264", {"start": v(-14.38, 1.63) * mm, "end": v(-10.36, 0) * mm});
            skLineSegment(sketch, "E265", {"start": v(-10.36, 0) * mm, "end": v(-9.97, -1.79) * mm});
            skLineSegment(sketch, "E266", {"start": v(-10.36, -11.75) * mm, "end": v(-15.77, -8.97) * mm});
            skLineSegment(sketch, "E267", {"start": v(-15.77, -8.97) * mm, "end": v(-15.77, -8.09) * mm});
            skLineSegment(sketch, "E268", {"start": v(-15.77, -8.09) * mm, "end": v(-10.36, -10.87) * mm});
            skLineSegment(sketch, "E269", {"start": v(-10.36, -10.87) * mm, "end": v(-10.36, -11.75) * mm});
            skLineSegment(sketch, "E270", {"start": v(-16.93, -25.61) * mm, "end": v(-16.93, -19.9) * mm});
            skLineSegment(sketch, "E271", {"start": v(-16.93, -19.9) * mm, "end": v(-15.77, -20.38) * mm});
            skLineSegment(sketch, "E272", {"start": v(-15.77, -20.38) * mm, "end": v(-16.28, -26.39) * mm});
            skLineSegment(sketch, "E273", {"start": v(-16.28, -26.39) * mm, "end": v(-16.93, -25.61) * mm});
            skLineSegment(sketch, "E274", {"start": v(-7.4, 15.33) * mm, "end": v(-12.34, 19.13) * mm});
            skLineSegment(sketch, "E275", {"start": v(-12.34, 19.13) * mm, "end": v(-11.81, 20.44) * mm});
            skLineSegment(sketch, "E276", {"start": v(-11.81, 20.44) * mm, "end": v(-6.07, 15.9) * mm});
            skLineSegment(sketch, "E277", {"start": v(-6.07, 15.9) * mm, "end": v(-7.4, 15.33) * mm});
            skLineSegment(sketch, "E278", {"start": v(-2.48, 20.46) * mm, "end": v(-5.56, 24.12) * mm});
            skLineSegment(sketch, "E279", {"start": v(-5.56, 24.12) * mm, "end": v(-5.48, 25.05) * mm});
            skLineSegment(sketch, "E280", {"start": v(-5.48, 25.05) * mm, "end": v(-1.74, 20.9) * mm});
            skLineSegment(sketch, "E281", {"start": v(-1.74, 20.9) * mm, "end": v(-2.48, 20.46) * mm});
            skLineSegment(sketch, "E282", {"start": v(-14.44, 34.66) * mm, "end": v(-19.81, 36.84) * mm});
            skLineSegment(sketch, "E283", {"start": v(-19.81, 36.84) * mm, "end": v(-19.37, 38.35) * mm});
            skLineSegment(sketch, "E284", {"start": v(-19.37, 38.35) * mm, "end": v(-14.23, 36.86) * mm});
            skLineSegment(sketch, "E285", {"start": v(-14.23, 36.86) * mm, "end": v(-14.44, 34.66) * mm});
            skLineSegment(sketch, "E286", {"start": v(-0.97, 19) * mm, "end": v(5.11, 26.06) * mm});
            skLineSegment(sketch, "E287", {"start": v(5.11, 26.06) * mm, "end": v(5.11, 24.33) * mm});
            skLineSegment(sketch, "E288", {"start": v(5.11, 24.33) * mm, "end": v(-0.78, 17.68) * mm});
            skLineSegment(sketch, "E289", {"start": v(-0.78, 17.68) * mm, "end": v(-0.97, 19) * mm});
            skLineSegment(sketch, "E290", {"start": v(14.92, 34.66) * mm, "end": v(20.36, 38.33) * mm});
            skLineSegment(sketch, "E291", {"start": v(20.36, 38.33) * mm, "end": v(19.26, 39.95) * mm});
            skLineSegment(sketch, "E292", {"start": v(19.26, 39.95) * mm, "end": v(14.7, 36.86) * mm});
            skLineSegment(sketch, "E293", {"start": v(14.7, 36.86) * mm, "end": v(14.92, 34.66) * mm});
            skLineSegment(sketch, "E294", {"start": v(27.39, 34.82) * mm, "end": v(22.91, 40.9) * mm});
            skLineSegment(sketch, "E295", {"start": v(22.91, 40.9) * mm, "end": v(24.4, 42) * mm});
            skLineSegment(sketch, "E296", {"start": v(24.4, 42) * mm, "end": v(29.7, 34.82) * mm});
            skLineSegment(sketch, "E297", {"start": v(29.7, 34.82) * mm, "end": v(27.39, 34.82) * mm});
            skLineSegment(sketch, "E298", {"start": v(27.39, 24.59) * mm, "end": v(25.47, 30.02) * mm});
            skLineSegment(sketch, "E299", {"start": v(25.47, 30.02) * mm, "end": v(27.39, 31.44) * mm});
            skLineSegment(sketch, "E300", {"start": v(27.39, 31.44) * mm, "end": v(29.92, 24.26) * mm});
            skLineSegment(sketch, "E301", {"start": v(29.92, 24.26) * mm, "end": v(27.39, 24.59) * mm});
            skLineSegment(sketch, "E302", {"start": v(29.92, 12.6) * mm, "end": v(27.39, 19.77) * mm});
            skLineSegment(sketch, "E303", {"start": v(27.39, 19.77) * mm, "end": v(28.58, 20.65) * mm});
            skLineSegment(sketch, "E304", {"start": v(28.58, 20.65) * mm, "end": v(31.42, 12.6) * mm});
            skLineSegment(sketch, "E305", {"start": v(31.42, 12.6) * mm, "end": v(29.92, 12.6) * mm});
            skLineSegment(sketch, "E306", {"start": v(31.42, 0) * mm, "end": v(28.58, 8.06) * mm});
            skLineSegment(sketch, "E307", {"start": v(28.58, 8.06) * mm, "end": v(29.92, 9.04) * mm});
            skLineSegment(sketch, "E308", {"start": v(29.92, 9.04) * mm, "end": v(33.11, 0) * mm});
            skLineSegment(sketch, "E309", {"start": v(33.11, 0) * mm, "end": v(31.42, 0) * mm});
            skLineSegment(sketch, "E310", {"start": v(28.58, -11.84) * mm, "end": v(28.58, -4.24) * mm});
            skLineSegment(sketch, "E311", {"start": v(28.58, -4.24) * mm, "end": v(29.92, -3.25) * mm});
            skLineSegment(sketch, "E312", {"start": v(29.92, -3.25) * mm, "end": v(29.92, -12.41) * mm});
            skLineSegment(sketch, "E313", {"start": v(29.92, -12.41) * mm, "end": v(28.58, -11.84) * mm});
            skLineSegment(sketch, "E314", {"start": v(27.39, -22.57) * mm, "end": v(27.39, -15.42) * mm});
            skLineSegment(sketch, "E315", {"start": v(27.39, -15.42) * mm, "end": v(28.58, -15.58) * mm});
            skLineSegment(sketch, "E316", {"start": v(28.58, -15.58) * mm, "end": v(28.58, -22.82) * mm});
            skLineSegment(sketch, "E317", {"start": v(28.58, -22.82) * mm, "end": v(27.39, -22.57) * mm});
            skLineSegment(sketch, "E318", {"start": v(17.82, -42.54) * mm, "end": v(19.9, -36.07) * mm});
            skLineSegment(sketch, "E319", {"start": v(19.9, -36.07) * mm, "end": v(21.22, -36.24) * mm});
            skLineSegment(sketch, "E320", {"start": v(21.22, -36.24) * mm, "end": v(19.15, -43.68) * mm});
            skLineSegment(sketch, "E321", {"start": v(19.15, -43.68) * mm, "end": v(17.82, -42.54) * mm});
            skLineSegment(sketch, "E322", {"start": v(23.58, -32.4) * mm, "end": v(23.58, -25.75) * mm});
            skLineSegment(sketch, "E323", {"start": v(23.58, -25.75) * mm, "end": v(25.47, -26) * mm});
            skLineSegment(sketch, "E324", {"start": v(25.47, -26) * mm, "end": v(25.47, -32.79) * mm});
            skLineSegment(sketch, "E325", {"start": v(25.47, -32.79) * mm, "end": v(23.58, -32.4) * mm});
            skLineSegment(sketch, "E326", {"start": v(16.56, -50.46) * mm, "end": v(15.03, -46.12) * mm});
            skLineSegment(sketch, "E327", {"start": v(15.03, -46.12) * mm, "end": v(16.73, -46.34) * mm});
            skLineSegment(sketch, "E328", {"start": v(16.73, -46.34) * mm, "end": v(18.4, -51.07) * mm});
            skLineSegment(sketch, "E329", {"start": v(18.4, -51.07) * mm, "end": v(16.56, -50.46) * mm});
            skLineSegment(sketch, "E330", {"start": v(12.86, -46.34) * mm, "end": v(5.81, -47.65) * mm});
            skLineSegment(sketch, "E331", {"start": v(5.81, -47.65) * mm, "end": v(5.81, -46.12) * mm});
            skLineSegment(sketch, "E332", {"start": v(5.81, -46.12) * mm, "end": v(13.58, -44.42) * mm});
            skLineSegment(sketch, "E333", {"start": v(13.58, -44.42) * mm, "end": v(12.86, -46.34) * mm});
            skLineSegment(sketch, "E334", {"start": v(3.23, -46.12) * mm, "end": v(5.33, -39.6) * mm});
            skLineSegment(sketch, "E335", {"start": v(5.33, -39.6) * mm, "end": v(6.63, -39.76) * mm});
            skLineSegment(sketch, "E336", {"start": v(6.63, -39.76) * mm, "end": v(4.26, -47.1) * mm});
            skLineSegment(sketch, "E337", {"start": v(4.26, -47.1) * mm, "end": v(3.23, -46.12) * mm});
            skLineSegment(sketch, "E338", {"start": v(8.93, -37.94) * mm, "end": v(8.93, -31.3) * mm});
            skLineSegment(sketch, "E339", {"start": v(8.93, -31.3) * mm, "end": v(10.19, -30.36) * mm});
            skLineSegment(sketch, "E340", {"start": v(10.19, -30.36) * mm, "end": v(10.19, -38.14) * mm});
            skLineSegment(sketch, "E341", {"start": v(10.19, -38.14) * mm, "end": v(8.93, -37.94) * mm});
            skLineSegment(sketch, "E342", {"start": v(11.2, -29.2) * mm, "end": v(11.2, -22.57) * mm});
            skLineSegment(sketch, "E343", {"start": v(11.2, -22.57) * mm, "end": v(12.86, -21.36) * mm});
            skLineSegment(sketch, "E344", {"start": v(12.86, -21.36) * mm, "end": v(12.86, -29.4) * mm});
            skLineSegment(sketch, "E345", {"start": v(12.86, -29.4) * mm, "end": v(11.2, -29.2) * mm});
            skLineSegment(sketch, "E346", {"start": v(12.86, -19.68) * mm, "end": v(12.86, -10.55) * mm});
            skLineSegment(sketch, "E347", {"start": v(12.86, -10.55) * mm, "end": v(15.03, -8.96) * mm});
            skLineSegment(sketch, "E348", {"start": v(15.03, -8.96) * mm, "end": v(15.03, -19.43) * mm});
            skLineSegment(sketch, "E349", {"start": v(15.03, -19.43) * mm, "end": v(12.86, -19.68) * mm});
            skLineSegment(sketch, "E350", {"start": v(15.03, -7.49) * mm, "end": v(13.63, 0) * mm});
            skLineSegment(sketch, "E351", {"start": v(13.63, 0) * mm, "end": v(15.03, 1.03) * mm});
            skLineSegment(sketch, "E352", {"start": v(15.03, 1.03) * mm, "end": v(16.56, -7.2) * mm});
            skLineSegment(sketch, "E353", {"start": v(16.56, -7.2) * mm, "end": v(15.03, -7.49) * mm});
            skLineSegment(sketch, "E354", {"start": v(15.03, 2.87) * mm, "end": v(12.86, 9) * mm});
            skLineSegment(sketch, "E355", {"start": v(12.86, 9) * mm, "end": v(15.03, 10.6) * mm});
            skLineSegment(sketch, "E356", {"start": v(15.03, 10.6) * mm, "end": v(16.56, 3.55) * mm});
            skLineSegment(sketch, "E357", {"start": v(16.56, 3.55) * mm, "end": v(15.03, 2.87) * mm});
            skLineSegment(sketch, "E358", {"start": v(12.86, 10.39) * mm, "end": v(11.2, 17.98) * mm});
            skLineSegment(sketch, "E359", {"start": v(11.2, 17.98) * mm, "end": v(12.86, 19.2) * mm});
            skLineSegment(sketch, "E360", {"start": v(12.86, 19.2) * mm, "end": v(14.3, 11.43) * mm});
            skLineSegment(sketch, "E361", {"start": v(14.3, 11.43) * mm, "end": v(12.86, 10.39) * mm});
            skLineSegment(sketch, "E362", {"start": v(11.82, 21.75) * mm, "end": v(9.5, 28.31) * mm});
            skLineSegment(sketch, "E363", {"start": v(9.5, 28.31) * mm, "end": v(10.52, 29.06) * mm});
            skLineSegment(sketch, "E364", {"start": v(10.52, 29.06) * mm, "end": v(12.86, 22.42) * mm});
            skLineSegment(sketch, "E365", {"start": v(11.82, 21.75) * mm, "end": v(12.86, 22.42) * mm});
            skLineSegment(sketch, "E366", {"start": v(-3.13, 6.66) * mm, "end": v(-5.2, 12.88) * mm});
            skLineSegment(sketch, "E367", {"start": v(-5.2, 12.88) * mm, "end": v(-4.33, 13.9) * mm});
            skLineSegment(sketch, "E368", {"start": v(-4.33, 13.9) * mm, "end": v(-1.78, 7.37) * mm});
            skLineSegment(sketch, "E369", {"start": v(-1.78, 7.37) * mm, "end": v(-3.13, 6.66) * mm});
            skLineSegment(sketch, "E370", {"start": v(-4.06, -3.85) * mm, "end": v(-6.72, 1.1) * mm});
            skLineSegment(sketch, "E371", {"start": v(-6.72, 1.1) * mm, "end": v(-5.69, 2.3) * mm});
            skLineSegment(sketch, "E372", {"start": v(-5.69, 2.3) * mm, "end": v(-3.13, -3.66) * mm});
            skLineSegment(sketch, "E373", {"start": v(-3.13, -3.66) * mm, "end": v(-4.06, -3.85) * mm});
            skLineSegment(sketch, "E374", {"start": v(1.4, 10.32) * mm, "end": v(6.91, 13.93) * mm});
            skLineSegment(sketch, "E375", {"start": v(6.91, 13.93) * mm, "end": v(6.22, 14.52) * mm});
            skLineSegment(sketch, "E376", {"start": v(6.22, 14.52) * mm, "end": v(1.4, 11.27) * mm});
            skLineSegment(sketch, "E377", {"start": v(1.4, 11.27) * mm, "end": v(1.4, 10.32) * mm});
            skLineSegment(sketch, "E378", {"start": v(0, -0.77) * mm, "end": v(6.87, 5.56) * mm});
            skLineSegment(sketch, "E379", {"start": v(6.87, 5.56) * mm, "end": v(6.87, 3.75) * mm});
            skLineSegment(sketch, "E380", {"start": v(6.87, 3.75) * mm, "end": v(0, -2.01) * mm});
            skLineSegment(sketch, "E381", {"start": v(0, -2.01) * mm, "end": v(0, -0.77) * mm});
            skLineSegment(sketch, "E382", {"start": v(2.55, -8.48) * mm, "end": v(10.52, -3.85) * mm});
            skLineSegment(sketch, "E383", {"start": v(10.52, -3.85) * mm, "end": v(9.96, -2.25) * mm});
            skLineSegment(sketch, "E384", {"start": v(9.96, -2.25) * mm, "end": v(2.11, -7.45) * mm});
            skLineSegment(sketch, "E385", {"start": v(2.11, -7.45) * mm, "end": v(2.55, -8.48) * mm});
            skLineSegment(sketch, "E386", {"start": v(-3.13, -11.84) * mm, "end": v(-4.88, -6.9) * mm});
            skLineSegment(sketch, "E387", {"start": v(-4.88, -6.9) * mm, "end": v(-4.06, -5.95) * mm});
            skLineSegment(sketch, "E388", {"start": v(-4.06, -5.95) * mm, "end": v(-1.98, -11.84) * mm});
            skLineSegment(sketch, "E389", {"start": v(-1.98, -11.84) * mm, "end": v(-3.13, -11.84) * mm});
            skLineSegment(sketch, "E390", {"start": v(-4.06, -21.61) * mm, "end": v(-5.4, -15.42) * mm});
            skLineSegment(sketch, "E391", {"start": v(-5.4, -15.42) * mm, "end": v(-4.06, -14.64) * mm});
            skLineSegment(sketch, "E392", {"start": v(-4.06, -14.64) * mm, "end": v(-2.66, -21.08) * mm});
            skLineSegment(sketch, "E393", {"start": v(-2.66, -21.08) * mm, "end": v(-4.06, -21.61) * mm});
            skLineSegment(sketch, "E394", {"start": v(-2.63, -27.92) * mm, "end": v(-3.66, -23.18) * mm});
            skLineSegment(sketch, "E395", {"start": v(-3.66, -23.18) * mm, "end": v(-2.63, -22.5) * mm});
            skLineSegment(sketch, "E396", {"start": v(-2.63, -22.5) * mm, "end": v(-1.54, -27.52) * mm});
            skLineSegment(sketch, "E397", {"start": v(-1.54, -27.52) * mm, "end": v(-2.63, -27.92) * mm});
            skLineSegment(sketch, "E398", {"start": v(-6.08, -36.72) * mm, "end": v(-6.08, -30.88) * mm});
            skLineSegment(sketch, "E399", {"start": v(-6.08, -30.88) * mm, "end": v(-5.34, -30.45) * mm});
            skLineSegment(sketch, "E400", {"start": v(-5.34, -30.45) * mm, "end": v(-5.34, -36.9) * mm});
            skLineSegment(sketch, "E401", {"start": v(-5.34, -36.9) * mm, "end": v(-6.08, -36.72) * mm});
            skLineSegment(sketch, "E402", {"start": v(-14.6, -20.24) * mm, "end": v(-11.44, -21.18) * mm});
            skLineSegment(sketch, "E403", {"start": v(-11.44, -21.18) * mm, "end": v(-11.44, -20.51) * mm});
            skLineSegment(sketch, "E404", {"start": v(-11.44, -20.51) * mm, "end": v(-14.87, -19.43) * mm});
            skLineSegment(sketch, "E405", {"start": v(-14.87, -19.43) * mm, "end": v(-14.6, -20.24) * mm});
            skLineSegment(sketch, "E406", {"start": v(-16.18, -27.92) * mm, "end": v(-10.36, -27.92) * mm});
            skLineSegment(sketch, "E407", {"start": v(-10.36, -27.92) * mm, "end": v(-10.8, -27.16) * mm});
            skLineSegment(sketch, "E408", {"start": v(-10.8, -27.16) * mm, "end": v(-16.18, -27.16) * mm});
            skLineSegment(sketch, "E409", {"start": v(-16.18, -27.16) * mm, "end": v(-16.18, -27.92) * mm});
            skLineSegment(sketch, "E410", {"start": v(-18.32, -36.22) * mm, "end": v(-11.77, -35.43) * mm});
            skLineSegment(sketch, "E411", {"start": v(-11.77, -35.43) * mm, "end": v(-12, -34.41) * mm});
            skLineSegment(sketch, "E412", {"start": v(-12, -34.41) * mm, "end": v(-18.44, -34.98) * mm});
            skLineSegment(sketch, "E413", {"start": v(-18.44, -34.98) * mm, "end": v(-18.32, -36.22) * mm});
            skLineSegment(sketch, "E414", {"start": v(-20.57, -44.32) * mm, "end": v(-14.97, -43.1) * mm});
            skLineSegment(sketch, "E415", {"start": v(-14.97, -43.1) * mm, "end": v(-15.25, -42.32) * mm});
            skLineSegment(sketch, "E416", {"start": v(-15.25, -42.32) * mm, "end": v(-20.76, -43.52) * mm});
            skLineSegment(sketch, "E417", {"start": v(-20.76, -43.52) * mm, "end": v(-20.57, -44.32) * mm});
            skLineSegment(sketch, "E418", {"start": v(-7.18, -43.07) * mm, "end": v(-7.95, -39.56) * mm});
            skLineSegment(sketch, "E419", {"start": v(-7.95, -39.56) * mm, "end": v(-7.23, -39.15) * mm});
            skLineSegment(sketch, "E420", {"start": v(-7.23, -39.15) * mm, "end": v(-6.36, -43.17) * mm});
            skLineSegment(sketch, "E421", {"start": v(-6.36, -43.17) * mm, "end": v(-7.18, -43.07) * mm});
            skLineSegment(sketch, "E422", {"start": v(-13.72, -46.56) * mm, "end": v(-13.72, -42.11) * mm});
            skLineSegment(sketch, "E423", {"start": v(-13.72, -42.11) * mm, "end": v(-12.85, -42.11) * mm});
            skLineSegment(sketch, "E424", {"start": v(-12.85, -42.11) * mm, "end": v(-12.85, -46.82) * mm});
            skLineSegment(sketch, "E425", {"start": v(-12.85, -46.82) * mm, "end": v(-13.72, -46.56) * mm});
            skLineSegment(sketch, "E426", {"start": v(-1.14, -47.75) * mm, "end": v(-7.18, -45.92) * mm});
            skLineSegment(sketch, "E427", {"start": v(-7.18, -45.92) * mm, "end": v(-6.83, -44.76) * mm});
            skLineSegment(sketch, "E428", {"start": v(-6.83, -44.76) * mm, "end": v(0.72, -47.04) * mm});
            skLineSegment(sketch, "E429", {"start": v(0.72, -47.04) * mm, "end": v(-1.14, -47.75) * mm});
            skLineSegment(sketch, "E430", {"start": v(2.55, -42.12) * mm, "end": v(-5.02, -43.43) * mm});
            skLineSegment(sketch, "E431", {"start": v(-5.02, -43.43) * mm, "end": v(-5.02, -42.38) * mm});
            skLineSegment(sketch, "E432", {"start": v(-5.02, -42.38) * mm, "end": v(2.55, -41.25) * mm});
            skLineSegment(sketch, "E433", {"start": v(2.55, -41.25) * mm, "end": v(2.55, -42.12) * mm});
            skLineSegment(sketch, "E434", {"start": v(-2.63, -36.72) * mm, "end": v(5.11, -33.98) * mm});
            skLineSegment(sketch, "E435", {"start": v(5.11, -33.98) * mm, "end": v(4.42, -32.79) * mm});
            skLineSegment(sketch, "E436", {"start": v(4.42, -32.79) * mm, "end": v(-3.07, -35.43) * mm});
            skLineSegment(sketch, "E437", {"start": v(-3.07, -35.43) * mm, "end": v(-2.63, -36.72) * mm});
            skLineSegment(sketch, "E438", {"start": v(15.03, -43.53) * mm, "end": v(11.2, -38.65) * mm});
            skLineSegment(sketch, "E439", {"start": v(11.2, -38.65) * mm, "end": v(11.82, -37.94) * mm});
            skLineSegment(sketch, "E440", {"start": v(11.82, -37.94) * mm, "end": v(16.1, -43.07) * mm});
            skLineSegment(sketch, "E441", {"start": v(16.1, -43.07) * mm, "end": v(15.03, -43.53) * mm});
            skLineSegment(sketch, "E442", {"start": v(1.71, -26.83) * mm, "end": v(8.74, -23.98) * mm});
            skLineSegment(sketch, "E443", {"start": v(8.74, -23.98) * mm, "end": v(8.25, -22.77) * mm});
            skLineSegment(sketch, "E444", {"start": v(8.25, -22.77) * mm, "end": v(1.22, -25.62) * mm});
            skLineSegment(sketch, "E445", {"start": v(1.22, -25.62) * mm, "end": v(1.71, -26.83) * mm});
            skLineSegment(sketch, "E446", {"start": v(1.71, -19.02) * mm, "end": v(10.22, -14.08) * mm});
            skLineSegment(sketch, "E447", {"start": v(10.22, -14.08) * mm, "end": v(9.38, -12.63) * mm});
            skLineSegment(sketch, "E448", {"start": v(9.38, -12.63) * mm, "end": v(1.07, -17.46) * mm});
            skLineSegment(sketch, "E449", {"start": v(1.07, -17.46) * mm, "end": v(1.71, -19.02) * mm});
            skLineSegment(sketch, "E450", {"start": v(15.8, -28.05) * mm, "end": v(25.72, -24.05) * mm});
            skPoint(sketch, "E450.startSnap0", {"position": v(15.8, 7.07) * mm});
            skLineSegment(sketch, "E451", {"start": v(25.72, -24.05) * mm, "end": v(25.02, -23.22) * mm});
            skLineSegment(sketch, "E452", {"start": v(25.02, -23.22) * mm, "end": v(14.78, -26.83) * mm});
            skLineSegment(sketch, "E453", {"start": v(14.78, -26.83) * mm, "end": v(15.8, -28.05) * mm});
            skLineSegment(sketch, "E454", {"start": v(13.45, -36.07) * mm, "end": v(21.54, -35.1) * mm});
            skLineSegment(sketch, "E455", {"start": v(21.54, -35.1) * mm, "end": v(21.4, -33.98) * mm});
            skLineSegment(sketch, "E456", {"start": v(21.4, -33.98) * mm, "end": v(13.62, -35.36) * mm});
            skLineSegment(sketch, "E457", {"start": v(13.62, -35.36) * mm, "end": v(13.45, -36.07) * mm});
            skLineSegment(sketch, "E458", {"start": v(18.22, -19.34) * mm, "end": v(24.78, -17.64) * mm});
            skLineSegment(sketch, "E459", {"start": v(24.78, -17.64) * mm, "end": v(24.63, -16.43) * mm});
            skLineSegment(sketch, "E460", {"start": v(24.63, -16.43) * mm, "end": v(18.1, -17.98) * mm});
            skLineSegment(sketch, "E461", {"start": v(18.1, -17.98) * mm, "end": v(18.22, -19.34) * mm});
            skLineSegment(sketch, "E462", {"start": v(19.9, -6.75) * mm, "end": v(26.11, -4.56) * mm});
            skLineSegment(sketch, "E463", {"start": v(26.11, -4.56) * mm, "end": v(25.4, -2.77) * mm});
            skLineSegment(sketch, "E464", {"start": v(25.4, -2.77) * mm, "end": v(19.9, -4.98) * mm});
            skLineSegment(sketch, "E465", {"start": v(19.9, -4.98) * mm, "end": v(19.9, -6.75) * mm});
            skLineSegment(sketch, "E466", {"start": v(20.17, 4.84) * mm, "end": v(27.06, 8.06) * mm});
            skLineSegment(sketch, "E467", {"start": v(27.06, 8.06) * mm, "end": v(26.47, 9.32) * mm});
            skLineSegment(sketch, "E468", {"start": v(26.47, 9.32) * mm, "end": v(19.9, 6.25) * mm});
            skLineSegment(sketch, "E469", {"start": v(19.9, 6.25) * mm, "end": v(20.17, 4.84) * mm});
            skLineSegment(sketch, "E470", {"start": v(19.67, 14.59) * mm, "end": v(25.95, 18.25) * mm});
            skLineSegment(sketch, "E471", {"start": v(25.95, 18.25) * mm, "end": v(25.47, 19.06) * mm});
            skLineSegment(sketch, "E472", {"start": v(25.47, 19.06) * mm, "end": v(19.29, 15.46) * mm});
            skLineSegment(sketch, "E473", {"start": v(19.29, 15.46) * mm, "end": v(19.67, 14.59) * mm});
            skLineSegment(sketch, "E474", {"start": v(18.47, 26.51) * mm, "end": v(23.76, 29.6) * mm});
            skLineSegment(sketch, "E475", {"start": v(23.76, 29.6) * mm, "end": v(24.37, 28.55) * mm});
            skLineSegment(sketch, "E476", {"start": v(24.37, 28.55) * mm, "end": v(18.59, 25.18) * mm});
            skLineSegment(sketch, "E477", {"start": v(18.59, 25.18) * mm, "end": v(18.47, 26.51) * mm});
            skSolve(sketch);
        }
        {
            var Q0;
            Q0 = qSketchRegion(id + "F2", true);
            var Q1;
            Q1 = qSketchRegion(id + "F0", true);
            extrude(context, id + "F3", {"entities" : qUnion([Q0, Q1]), "operationType" : NewBodyOperationType.ADD, "depth" : 25.4 * mm, "offsetDistance" : 25.4 * mm});
        }
        {
            var Q0;
            Q0=makeQuery(id+"F1.opExtrude","CAP_FACE",FACE,{"disambiguationData":[OSD([sQuery(id+"F0.wireOp",EDGE,"E120"),sQuery(id+"F0.wireOp",EDGE,"E121"),sQuery(id+"F0.wireOp",EDGE,"E122"),sQuery(id+"F0.wireOp",EDGE,"E123"),sQuery(id+"F0.wireOp",EDGE,"E124"),sQuery(id+"F0.wireOp",EDGE,"E204.bottom")])],"isStart":false});
            var sketch = newSketch(context, id + "F4", { "sketchPlane" : qUnion([Q0])});
            skLineSegment(sketch, "E478", {"start": v(-34.56, 61.53) * mm, "end": v(2.48, 28.19) * mm});
            skLineSegment(sketch, "E479", {"start": v(2.48, 28.19) * mm, "end": v(-10.47, 15.2) * mm});
            skLineSegment(sketch, "E480", {"start": v(-10.47, 15.2) * mm, "end": v(-11.37, 14.2) * mm});
            skLineSegment(sketch, "E481", {"start": v(-11.37, 14.2) * mm, "end": v(-11.37, 3.23) * mm});
            skLineSegment(sketch, "E482", {"start": v(-11.37, 3.23) * mm, "end": v(-12.05, 1.42) * mm});
            skLineSegment(sketch, "E483", {"start": v(-12.05, 1.42) * mm, "end": v(-13.41, -14.11) * mm});
            skLineSegment(sketch, "E484", {"start": v(-13.41, -14.11) * mm, "end": v(-13.41, -32.34) * mm});
            skLineSegment(sketch, "E485", {"start": v(-13.41, -32.34) * mm, "end": v(-16.08, -39.45) * mm});
            skLineSegment(sketch, "E486", {"start": v(-16.08, -39.45) * mm, "end": v(-18.77, -46.62) * mm});
            skLineSegment(sketch, "E487", {"start": v(-18.77, -46.62) * mm, "end": v(-37.42, -47.81) * mm});
            skLineSegment(sketch, "E488", {"start": v(-37.42, -47.81) * mm, "end": v(-67.6, 42.75) * mm});
            skLineSegment(sketch, "E489", {"start": v(-67.6, 42.75) * mm, "end": v(-34.56, 61.53) * mm});
            skSolve(sketch);
        }
        {
            var Q0;
            Q0 = qSketchRegion(id + "F4", true);
            extrude(context, id + "F5", {"entities" : qUnion([Q0]), "operationType" : NewBodyOperationType.REMOVE, "oppositeDirection" : true, "depth" : 2.03 * mm, "offsetDistance" : 25.4 * mm});
        }
    });
